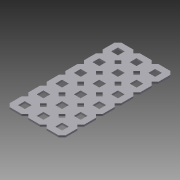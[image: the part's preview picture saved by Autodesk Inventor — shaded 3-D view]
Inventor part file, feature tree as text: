
AUTODESK INVENTOR PART (.ipt)
format: ipt  version: 2012 (Build 160160000, 160)  size: 1,057,792 bytes
history: native  units: in
note: dims shown in document units (in); Inventor stores cm internally (conversion verified against a paired STEP export)
features: sketch x2, other x1, imported_body x1, extrude x1
ambient origin geometry x8: Origin, YZ Plane, XZ Plane, XY Plane, X Axis, Y Axis, Z Axis, Center Point
feature tree (5):
  parser-record x1  (decoder bookkeeping rows leaked as tree rows — omitted from the tree; the rows remain in map.json)
  imported_body  "Base1"
  sketch  "Sketch1"  dims[d0=3.937in d2=0.5in d3=1.9685in d5=0.5in d10=1.0in d11=0.0in]
  extrude  "Extrusion1"  Depth=1.0in TaperAngle=0.0deg
  sketch  "Sketch3"
